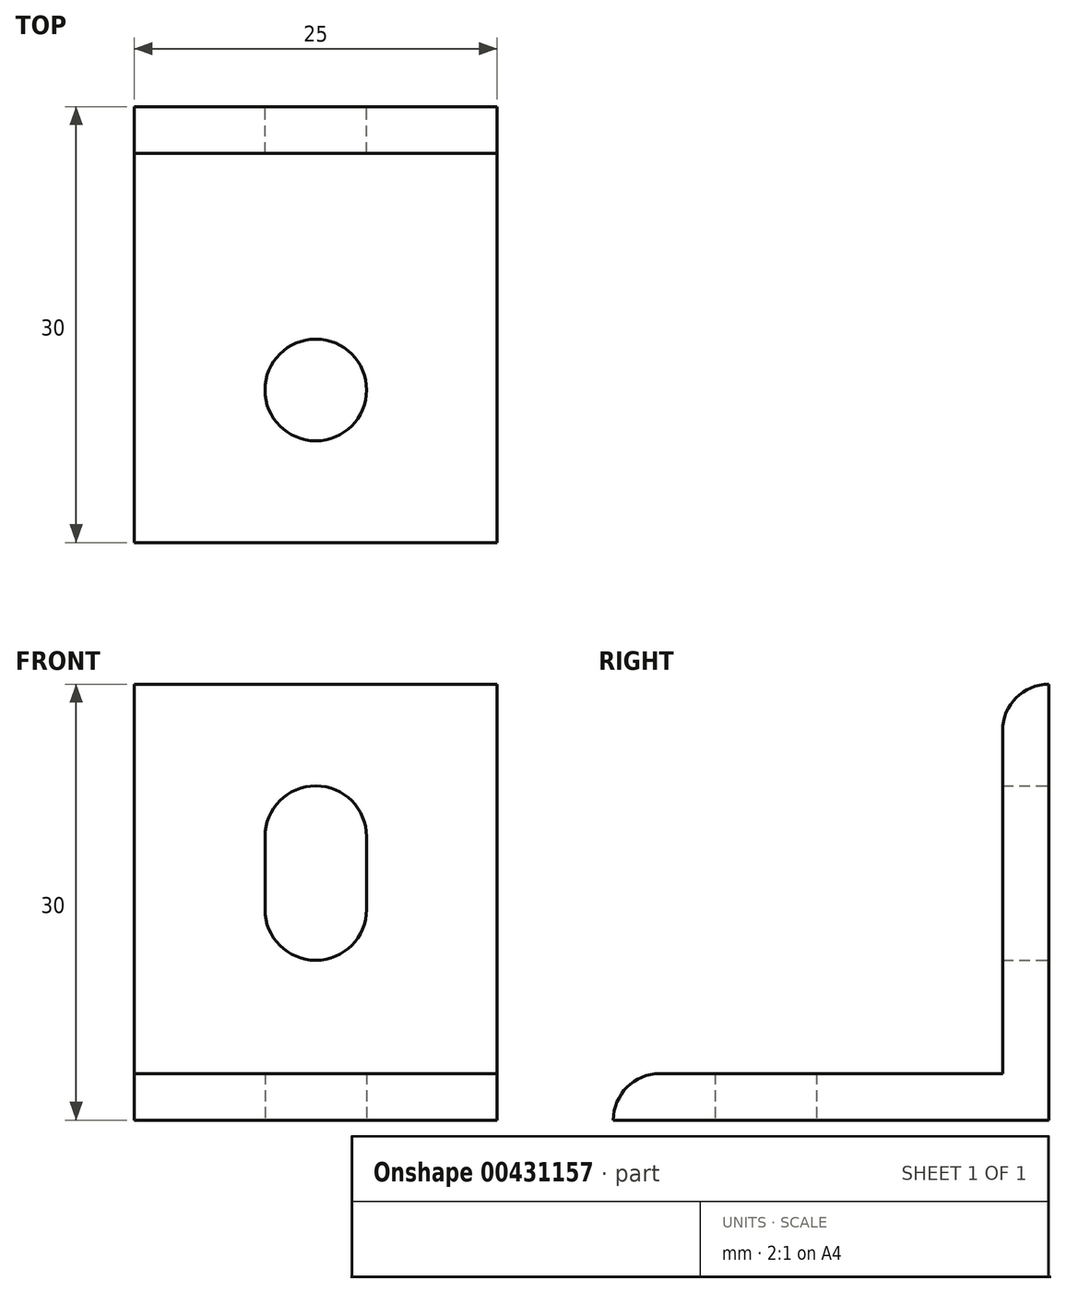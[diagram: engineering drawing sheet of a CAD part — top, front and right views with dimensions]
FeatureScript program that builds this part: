
annotation { "Feature Type Name" : "Feature", "Feature Type Description" : "" }
export const myFeature = defineFeature(function(context is Context, id is Id, definition is map)
    precondition{}
    {
        {
            var Q0;
            Q0=qCreatedBy(makeId("Top.planeOp"),FACE);
            var sketch = newSketch(context, id + "F0", { "sketchPlane" : qUnion([Q0])});
            skLineSegment(sketch, "E0.bottom", {"start": v(12.5, 15) * mm, "end": v(-12.5, 15) * mm});
            skLineSegment(sketch, "E0.top", {"start": v(12.5, -15) * mm, "end": v(-12.5, -15) * mm});
            skLineSegment(sketch, "E0.left", {"start": v(12.5, 15) * mm, "end": v(12.5, -15) * mm});
            skLineSegment(sketch, "E0.right", {"start": v(-12.5, 15) * mm, "end": v(-12.5, -15) * mm});
            skPoint(sketch, "E0.middle", {"position": v(0, 0) * mm});
            skLineSegment(sketch, "E1", {"start": v(0, 15) * mm, "end": v(0, -15) * mm, "construction": true});
            skCircle(sketch, "E2", {"center": v(0, -4.5) * mm, "radius": 3.5 * mm});
            skLineSegment(sketch, "E3", {"start": v(-12.5, 11.8) * mm, "end": v(12.5, 11.8) * mm});
            skSolve(sketch);
        }
        {
            var Q0;
            {var subQ1=sQuery(id+"F0.wireOp",EDGE,"E0.top");Q0=makeQuery(id+"F0.imprint","IMPRINT",FACE,{"disambiguationData":[TD([[makeQuery(id+"F0.imprint","IMPRINT",EDGE,{"derivedFrom":subQ1}),-1.0]])]});}
            extrude(context, id + "F1", {"entities" : qUnion([Q0]), "depth" : 3.2 * mm});
        }
        {
            var Q0;
            {var subQ0=sQuery(id+"F0.wireOp",EDGE,"E0.bottom");Q0=makeQuery(id+"F0.imprint","IMPRINT",FACE,{"disambiguationData":[TD([[makeQuery(id+"F0.imprint","IMPRINT",EDGE,{"derivedFrom":subQ0}),1.0]])]});}
            extrude(context, id + "F2", {"entities" : qUnion([Q0]), "operationType" : NewBodyOperationType.ADD, "depth" : 30 * mm});
        }
        {
            var Q0;
            Q0=makeQuery(id+"F2.opExtrude","SWEPT_FACE",FACE,{"disambiguationData":[OSD([sQuery(id+"F0.wireOp",EDGE,"E0.bottom")])]});
            var sketch = newSketch(context, id + "F3", { "sketchPlane" : qUnion([Q0])});
            skLineSegment(sketch, "E4", {"start": v(0, 19.5) * mm, "end": v(0, 14.5) * mm, "construction": true});
            skArc(sketch, "E5", {"start": v(-3.5, 14.5) * mm, "mid": v(0, 11) * mm, "end": v(3.5, 14.5) * mm});
            skLineSegment(sketch, "E6", {"start": v(-3.5, 19.5) * mm, "end": v(-3.5, 14.5) * mm});
            skLineSegment(sketch, "E7", {"start": v(3.5, 19.5) * mm, "end": v(3.5, 14.5) * mm});
            skArc(sketch, "E8.trimOffspring", {"start": v(3.5, 19.5) * mm, "mid": v(0, 23) * mm, "end": v(-3.5, 19.5) * mm});
            skSolve(sketch);
        }
        {
            var Q0;
            Q0=makeQuery(id+"F3.imprint","IMPRINT",FACE,{"disambiguationData":[TD([[makeQuery(id+"F3.imprint","IMPRINT",EDGE,{"derivedFrom":sQuery(id+"F3.wireOp",EDGE,"E5")}),1.0]])]});
            extrude(context, id + "F4", {"entities" : qUnion([Q0]), "operationType" : NewBodyOperationType.REMOVE, "oppositeDirection" : true, "depth" : 3.2 * mm});
        }
        {
            var Q0;
            Q0=makeQuery(id+"F2.opExtrude","CAP_EDGE",EDGE,{"disambiguationData":[OSD([sQuery(id+"F0.wireOp",EDGE,"E3")])],"isStart":false});
            fillet(context, id + "F5", {"entities" : qUnion([Q0]), "radius" : 3.2 * mm, "tangentPropagation" : true, "allowEdgeOverflow" : false});
        }
        {
            var Q0;
            Q0=makeQuery(id+"F1.opExtrude","CAP_EDGE",EDGE,{"disambiguationData":[OSD([sQuery(id+"F0.wireOp",EDGE,"E0.top")])],"isStart":false});
            fillet(context, id + "F6", {"entities" : qUnion([Q0]), "radius" : 3.2 * mm, "tangentPropagation" : true, "allowEdgeOverflow" : false});
        }
    });
